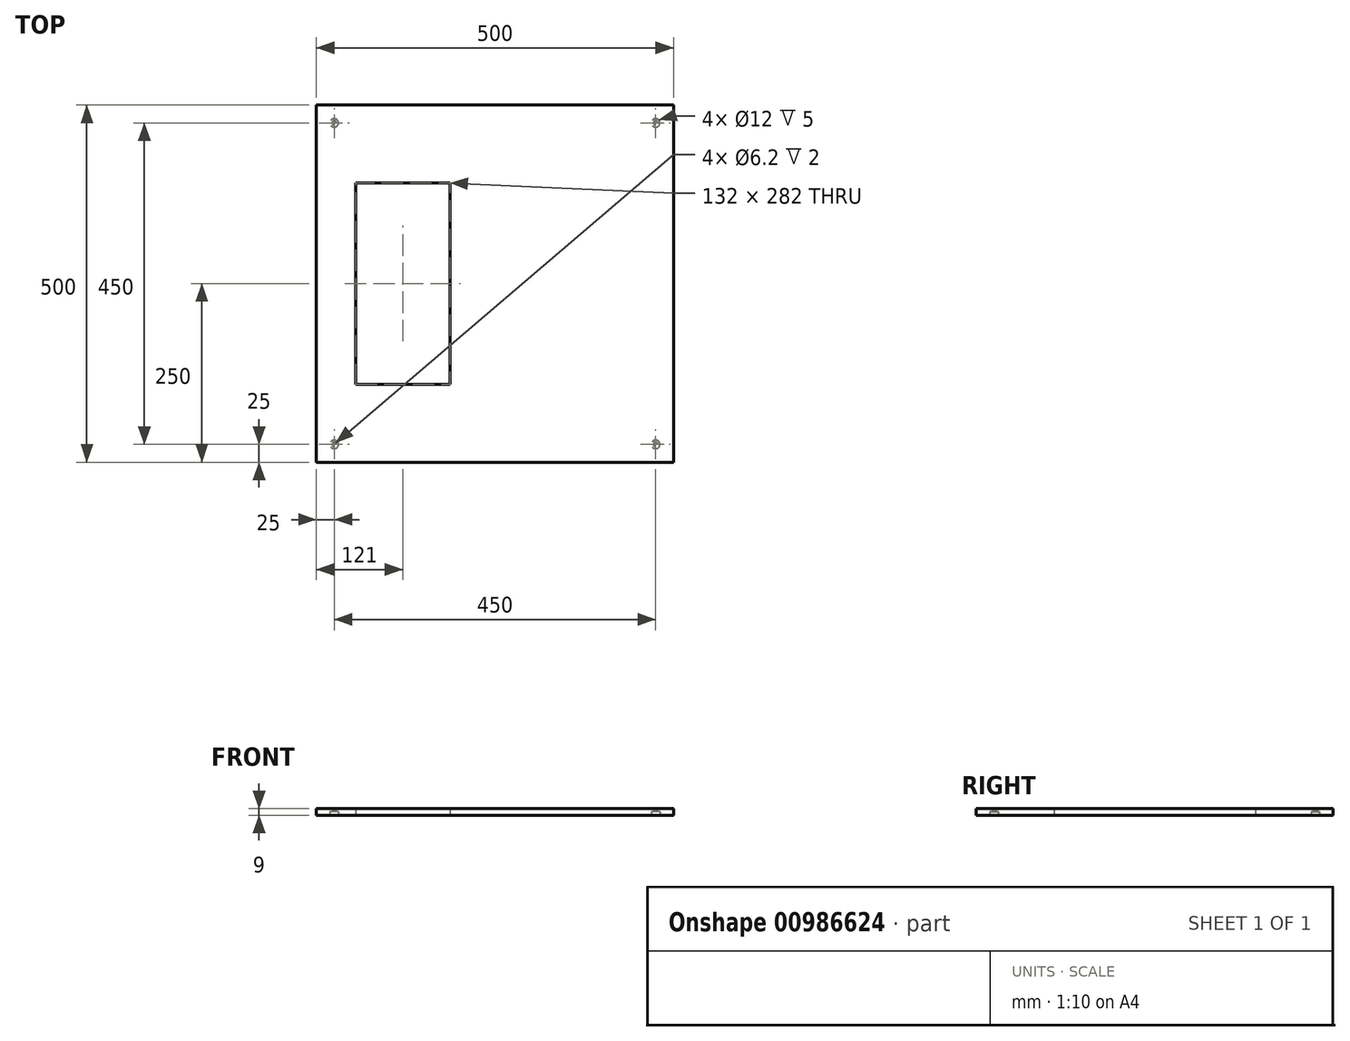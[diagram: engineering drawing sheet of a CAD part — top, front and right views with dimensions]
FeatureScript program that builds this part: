
annotation { "Feature Type Name" : "Feature", "Feature Type Description" : "" }
export const myFeature = defineFeature(function(context is Context, id is Id, definition is map)
    precondition{}
    {
        {
            var Q0;
            Q0=qCreatedBy(makeId("Top.planeOp"),FACE);
            var sketch = newSketch(context, id + "F0", { "sketchPlane" : qUnion([Q0])});
            skLineSegment(sketch, "E0.bottom", {"start": v(0, 500) * mm, "end": v(500, 500) * mm});
            skLineSegment(sketch, "E0.top", {"start": v(0, 0) * mm, "end": v(500, 0) * mm});
            skLineSegment(sketch, "E0.left", {"start": v(0, 500) * mm, "end": v(0, 0) * mm});
            skLineSegment(sketch, "E0.right", {"start": v(500, 500) * mm, "end": v(500, 0) * mm});
            skCircle(sketch, "E1", {"center": v(25, 475) * mm, "radius": 6 * mm});
            skCircle(sketch, "E2.0.1.0", {"center": v(25, 25) * mm, "radius": 6 * mm});
            skCircle(sketch, "E2.1.0.0", {"center": v(475, 475) * mm, "radius": 6 * mm});
            skCircle(sketch, "E2.1.1.0", {"center": v(475, 25) * mm, "radius": 6 * mm});
            skLineSegment(sketch, "E2.direction1", {"start": v(25, 475) * mm, "end": v(475, 475) * mm, "construction": true});
            skLineSegment(sketch, "E2.direction2", {"start": v(25, 475) * mm, "end": v(25, 25) * mm, "construction": true});
            skCircle(sketch, "E3", {"center": v(25, 475) * mm, "radius": 3.1 * mm});
            skCircle(sketch, "E4.0.1.0", {"center": v(25, 25) * mm, "radius": 3.1 * mm});
            skCircle(sketch, "E4.1.0.0", {"center": v(475, 475) * mm, "radius": 3.1 * mm});
            skCircle(sketch, "E4.1.1.0", {"center": v(475, 25) * mm, "radius": 3.1 * mm});
            skLineSegment(sketch, "E5.bottom", {"start": v(55, 391) * mm, "end": v(187, 391) * mm});
            skLineSegment(sketch, "E5.top", {"start": v(55, 109) * mm, "end": v(187, 109) * mm});
            skLineSegment(sketch, "E5.left", {"start": v(55, 391) * mm, "end": v(55, 109) * mm});
            skLineSegment(sketch, "E5.right", {"start": v(187, 391) * mm, "end": v(187, 109) * mm});
            skSolve(sketch);
        }
        {
            var Q0;
            Q0=makeQuery(id+"F0.imprint","IMPRINT",FACE,{"disambiguationData":[TD([[makeQuery(id+"F0.imprint","IMPRINT",EDGE,{"derivedFrom":sQuery(id+"F0.wireOp",EDGE,"E2.1.1.0")}),1.0]])]});
            var Q1;
            Q1=makeQuery(id+"F0.imprint","IMPRINT",FACE,{"disambiguationData":[TD([[makeQuery(id+"F0.imprint","IMPRINT",EDGE,{"derivedFrom":sQuery(id+"F0.wireOp",EDGE,"E2.0.1.0")}),1.0]])]});
            var Q2;
            Q2=makeQuery(id+"F0.imprint","IMPRINT",FACE,{"disambiguationData":[TD([[makeQuery(id+"F0.imprint","IMPRINT",EDGE,{"derivedFrom":sQuery(id+"F0.wireOp",EDGE,"E0.bottom")}),-1.0]])]});
            var Q3;
            Q3=makeQuery(id+"F0.imprint","IMPRINT",FACE,{"disambiguationData":[TD([[makeQuery(id+"F0.imprint","IMPRINT",EDGE,{"derivedFrom":sQuery(id+"F0.wireOp",EDGE,"E1")}),1.0]])]});
            var Q4;
            Q4=makeQuery(id+"F0.imprint","IMPRINT",FACE,{"disambiguationData":[TD([[makeQuery(id+"F0.imprint","IMPRINT",EDGE,{"derivedFrom":sQuery(id+"F0.wireOp",EDGE,"E2.1.0.0")}),1.0]])]});
            var Q5;
            Q5=makeQuery(id+"F0.imprint","IMPRINT",FACE,{"disambiguationData":[TD([[makeQuery(id+"F0.imprint","IMPRINT",EDGE,{"derivedFrom":sQuery(id+"F0.wireOp",EDGE,"E4.1.1.0")}),1.0]])]});
            var Q6;
            Q6=makeQuery(id+"F0.imprint","IMPRINT",FACE,{"disambiguationData":[TD([[makeQuery(id+"F0.imprint","IMPRINT",EDGE,{"derivedFrom":sQuery(id+"F0.wireOp",EDGE,"E4.1.0.0")}),1.0]])]});
            var Q7;
            Q7=makeQuery(id+"F0.imprint","IMPRINT",FACE,{"disambiguationData":[TD([[makeQuery(id+"F0.imprint","IMPRINT",EDGE,{"derivedFrom":sQuery(id+"F0.wireOp",EDGE,"E3")}),1.0]])]});
            var Q8;
            Q8=makeQuery(id+"F0.imprint","IMPRINT",FACE,{"disambiguationData":[TD([[makeQuery(id+"F0.imprint","IMPRINT",EDGE,{"derivedFrom":sQuery(id+"F0.wireOp",EDGE,"E4.0.1.0")}),1.0]])]});
            var Q9;
            Q9=makeQuery(id+"F0.imprint","IMPRINT",FACE,{"disambiguationData":[TD([[makeQuery(id+"F0.imprint","IMPRINT",EDGE,{"derivedFrom":sQuery(id+"F0.wireOp",EDGE,"E5.bottom")}),-1.0]])]});
            extrude(context, id + "F1", {"entities" : qUnion([Q0, Q1, Q2, Q3, Q4, Q5, Q6, Q7, Q8, Q9]), "depth" : 9 * mm, "offsetDistance" : 25 * mm});
        }
        {
            var Q0;
            Q0=makeQuery(id+"F0.imprint","IMPRINT",FACE,{"disambiguationData":[TD([[makeQuery(id+"F0.imprint","IMPRINT",EDGE,{"derivedFrom":sQuery(id+"F0.wireOp",EDGE,"E4.1.1.0")}),1.0]])]});
            var Q1;
            Q1=makeQuery(id+"F0.imprint","IMPRINT",FACE,{"disambiguationData":[TD([[makeQuery(id+"F0.imprint","IMPRINT",EDGE,{"derivedFrom":sQuery(id+"F0.wireOp",EDGE,"E4.1.0.0")}),1.0]])]});
            var Q2;
            Q2=makeQuery(id+"F0.imprint","IMPRINT",FACE,{"disambiguationData":[TD([[makeQuery(id+"F0.imprint","IMPRINT",EDGE,{"derivedFrom":sQuery(id+"F0.wireOp",EDGE,"E3")}),1.0]])]});
            var Q3;
            Q3=makeQuery(id+"F0.imprint","IMPRINT",FACE,{"disambiguationData":[TD([[makeQuery(id+"F0.imprint","IMPRINT",EDGE,{"derivedFrom":sQuery(id+"F0.wireOp",EDGE,"E4.0.1.0")}),1.0]])]});
            extrude(context, id + "F2", {"entities" : qUnion([Q0, Q1, Q2, Q3]), "operationType" : NewBodyOperationType.REMOVE, "depth" : 7 * mm, "offsetDistance" : 25 * mm});
        }
        {
            var Q0;
            Q0=makeQuery(id+"F0.imprint","IMPRINT",FACE,{"disambiguationData":[TD([[makeQuery(id+"F0.imprint","IMPRINT",EDGE,{"derivedFrom":sQuery(id+"F0.wireOp",EDGE,"E2.1.0.0")}),1.0]])]});
            var Q1;
            Q1=makeQuery(id+"F0.imprint","IMPRINT",FACE,{"disambiguationData":[TD([[makeQuery(id+"F0.imprint","IMPRINT",EDGE,{"derivedFrom":sQuery(id+"F0.wireOp",EDGE,"E1")}),1.0]])]});
            var Q2;
            Q2=makeQuery(id+"F0.imprint","IMPRINT",FACE,{"disambiguationData":[TD([[makeQuery(id+"F0.imprint","IMPRINT",EDGE,{"derivedFrom":sQuery(id+"F0.wireOp",EDGE,"E2.0.1.0")}),1.0]])]});
            var Q3;
            Q3=makeQuery(id+"F0.imprint","IMPRINT",FACE,{"disambiguationData":[TD([[makeQuery(id+"F0.imprint","IMPRINT",EDGE,{"derivedFrom":sQuery(id+"F0.wireOp",EDGE,"E2.1.1.0")}),1.0]])]});
            extrude(context, id + "F3", {"entities" : qUnion([Q0, Q1, Q2, Q3]), "operationType" : NewBodyOperationType.REMOVE, "depth" : 5 * mm, "offsetDistance" : 25 * mm});
        }
        {
            var Q0;
            Q0=makeQuery(id+"F0.imprint","IMPRINT",FACE,{"disambiguationData":[TD([[makeQuery(id+"F0.imprint","IMPRINT",EDGE,{"derivedFrom":sQuery(id+"F0.wireOp",EDGE,"E5.bottom")}),-1.0]])]});
            extrude(context, id + "F4", {"entities" : qUnion([Q0]), "operationType" : NewBodyOperationType.REMOVE, "depth" : 25 * mm, "offsetDistance" : 25 * mm});
        }
    });
